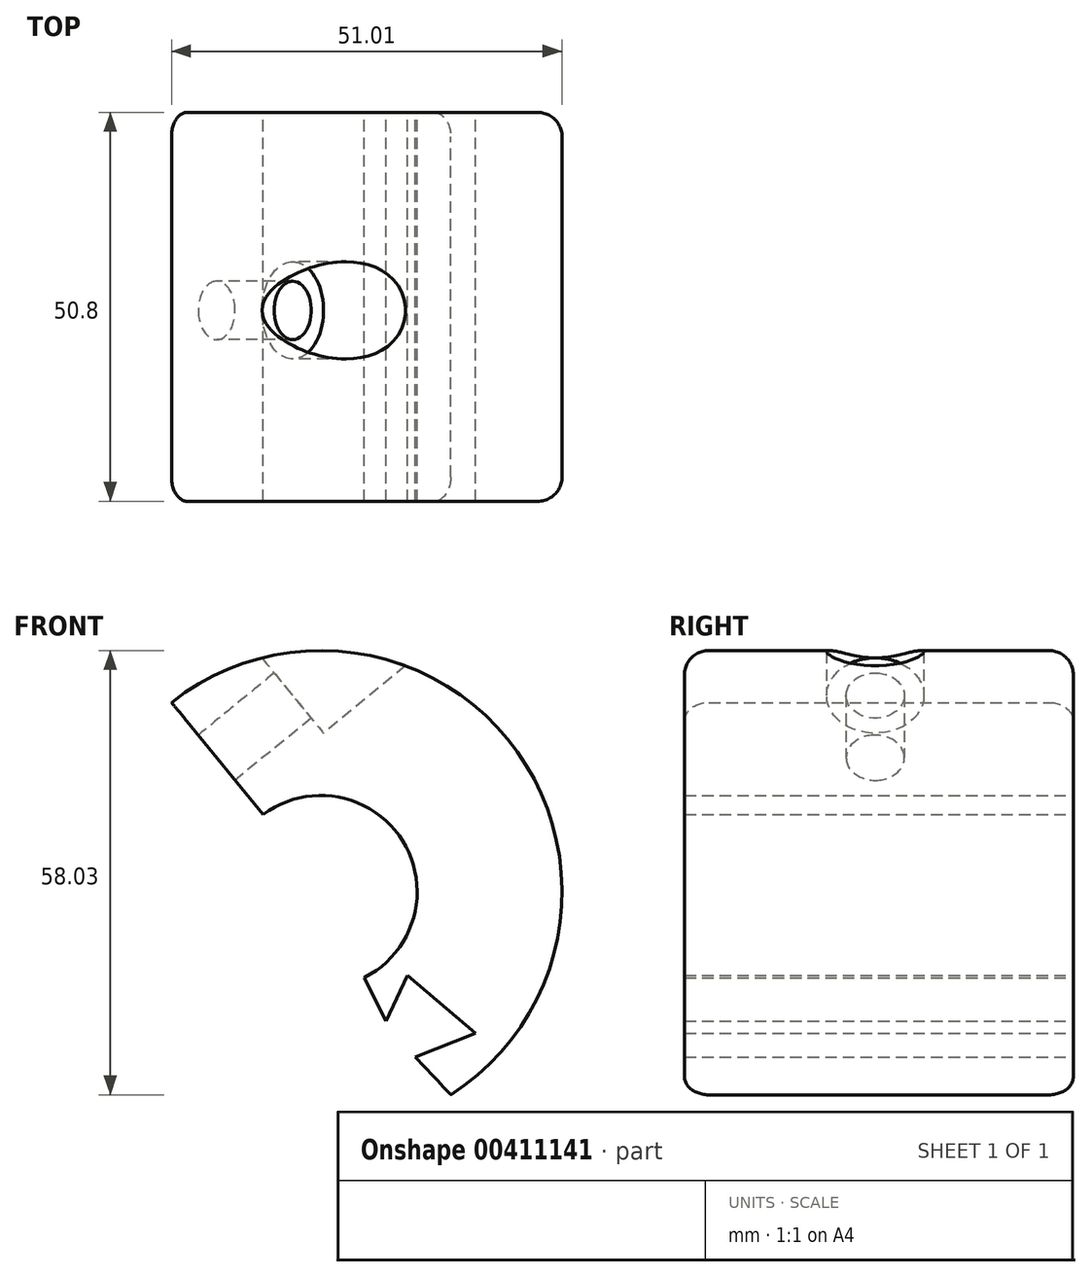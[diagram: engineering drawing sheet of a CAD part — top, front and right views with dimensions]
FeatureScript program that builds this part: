
annotation { "Feature Type Name" : "Feature", "Feature Type Description" : "" }
export const myFeature = defineFeature(function(context is Context, id is Id, definition is map)
    precondition{}
    {
        {
            var Q0;
            Q0=qCreatedBy(makeId("Front.planeOp"),FACE);
            var sketch = newSketch(context, id + "F0", { "sketchPlane" : qUnion([Q0])});
            skArc(sketch, "E0", {"start": v(16.52, -13.48) * mm, "mid": v(21.5, 4.36) * mm, "end": v(3.28, 7.79) * mm});
            skArc(sketch, "E1", {"start": v(27.79, -28.81) * mm, "mid": v(36.47, 15.99) * mm, "end": v(-8.7, 22.44) * mm});
            skLineSegment(sketch, "E2.right", {"start": v(-48.9, -37.54) * mm, "end": v(-48.9, -37.55) * mm});
            skLineSegment(sketch, "E3", {"start": v(-8.7, 22.44) * mm, "end": v(3.28, 7.79) * mm});
            skLineSegment(sketch, "E4", {"start": v(22.17, -13.25) * mm, "end": v(22.2, -13.19) * mm});
            skLineSegment(sketch, "E5", {"start": v(16.52, -13.48) * mm, "end": v(16.46, -13.51) * mm});
            skLineSegment(sketch, "E6", {"start": v(16.46, -13.51) * mm, "end": v(19.33, -19.2) * mm});
            skLineSegment(sketch, "E7", {"start": v(19.33, -19.2) * mm, "end": v(22.11, -13.2) * mm});
            skLineSegment(sketch, "E8", {"start": v(22.11, -13.2) * mm, "end": v(31, -20.8) * mm});
            skLineSegment(sketch, "E9", {"start": v(31, -20.8) * mm, "end": v(23.16, -23.85) * mm});
            skPoint(sketch, "E10.end.orphan", {"position": v(19.4, -19.2) * mm});
            skLineSegment(sketch, "E11", {"start": v(23.16, -23.85) * mm, "end": v(27.79, -28.81) * mm});
            skSolve(sketch);
        }
        {
            var Q0;
            Q0=makeQuery(id+"F0.imprint","IMPRINT",FACE,{"disambiguationData":[TD([[makeQuery(id+"F0.imprint","IMPRINT",EDGE,{"derivedFrom":sQuery(id+"F0.wireOp",EDGE,"E0")}),-1.0]])]});
            extrude(context, id + "F1", {"entities" : qUnion([Q0]), "flatOperationType" : FlatOperationType.REMOVE, "offsetDistance" : 25.4 * mm, "depth" : 50.8 * mm, "domain" : OperationDomain.MODEL});
        }
        {
            var Q0;
            Q0=makeQuery(id+"F1.opExtrude","SWEPT_FACE",FACE,{"disambiguationData":[OSD([sQuery(id+"F0.wireOp",EDGE,"E3")])]});
            cPlane(context, id + "F2", {"entities" : qUnion([Q0]), "cplaneType" : CPlaneType.OFFSET, "offset" : 28.57 * mm, "oppositeDirection" : true, "width" : 152.4 * mm, "height" : 152.4 * mm});
        }
        {
            var Q0;
            Q0=qCreatedBy(id+"F2.planeOp",FACE);
            var sketch = newSketch(context, id + "F3", { "sketchPlane" : qUnion([Q0])});
            skPoint(sketch, "E12", {"position": v(25.87, 13.55) * mm});
            skSolve(sketch);
        }
        {
            var Q0;
            Q0=sQuery(id+"F3.wireOp",VERTEX,"E12");
            var Q1;
            Q1=makeQuery(id+"F1.opExtrude","SWEPT_BODY",BODY,{"disambiguationData":[OSD([sQuery(id+"F0.wireOp",EDGE,"E0"),sQuery(id+"F0.wireOp",EDGE,"E1"),sQuery(id+"F0.wireOp",EDGE,"c0ffc589-c2a8-42a5-9104-419b5ff6041c"),sQuery(id+"F0.wireOp",EDGE,"134b5414-d073-441e-a36f-09c414d7f6e8"),sQuery(id+"F0.wireOp",EDGE,"2d02ed2d-40de-400d-b0a8-8be9bce04ba1"),sQuery(id+"F0.wireOp",EDGE,"35546e3c-a2fd-4c8c-8f61-3374b4d5c807"),sQuery(id+"F0.wireOp",EDGE,"078a7960-2e83-4ff7-9b07-46c6e9269b80"),sQuery(id+"F0.wireOp",EDGE,"E3")])]});
            hole(context, id + "F4", {"style" : HoleStyle.C_BORE, "endStyle" : HoleEndStyle.BLIND, "oppositeDirection" : true, "holeDiameter" : 7.62 * mm, "cBoreDiameter" : 12.7 * mm, "cBoreDepth" : 0 * mm, "majorDiameter" : 6.35 * mm, "holeDepth" : 25.4 * mm, "isTappedThrough" : true, "tappedDepth" : 12.7 * mm, "tapClearance" : 3, "locations" : qUnion([Q0]), "scope" : qUnion([Q1]), "startStyle" : HoleStartStyle.PART});
        }
        {
            var Q0;
            Q0=makeQuery(id+"F1.opExtrude","CAP_EDGE",EDGE,{"disambiguationData":[OSD([sQuery(id+"F0.wireOp",EDGE,"E1")])],"isStart":false});
            var Q1;
            Q1=makeQuery(id+"F1.opExtrude","CAP_EDGE",EDGE,{"disambiguationData":[OSD([sQuery(id+"F0.wireOp",EDGE,"E1")])],"isStart":true});
            fillet(context, id + "F5", {"entities" : qUnion([Q0, Q1]), "radius" : 3.17 * mm, "tangentPropagation" : true, "allowEdgeOverflow" : false});
        }
    });
